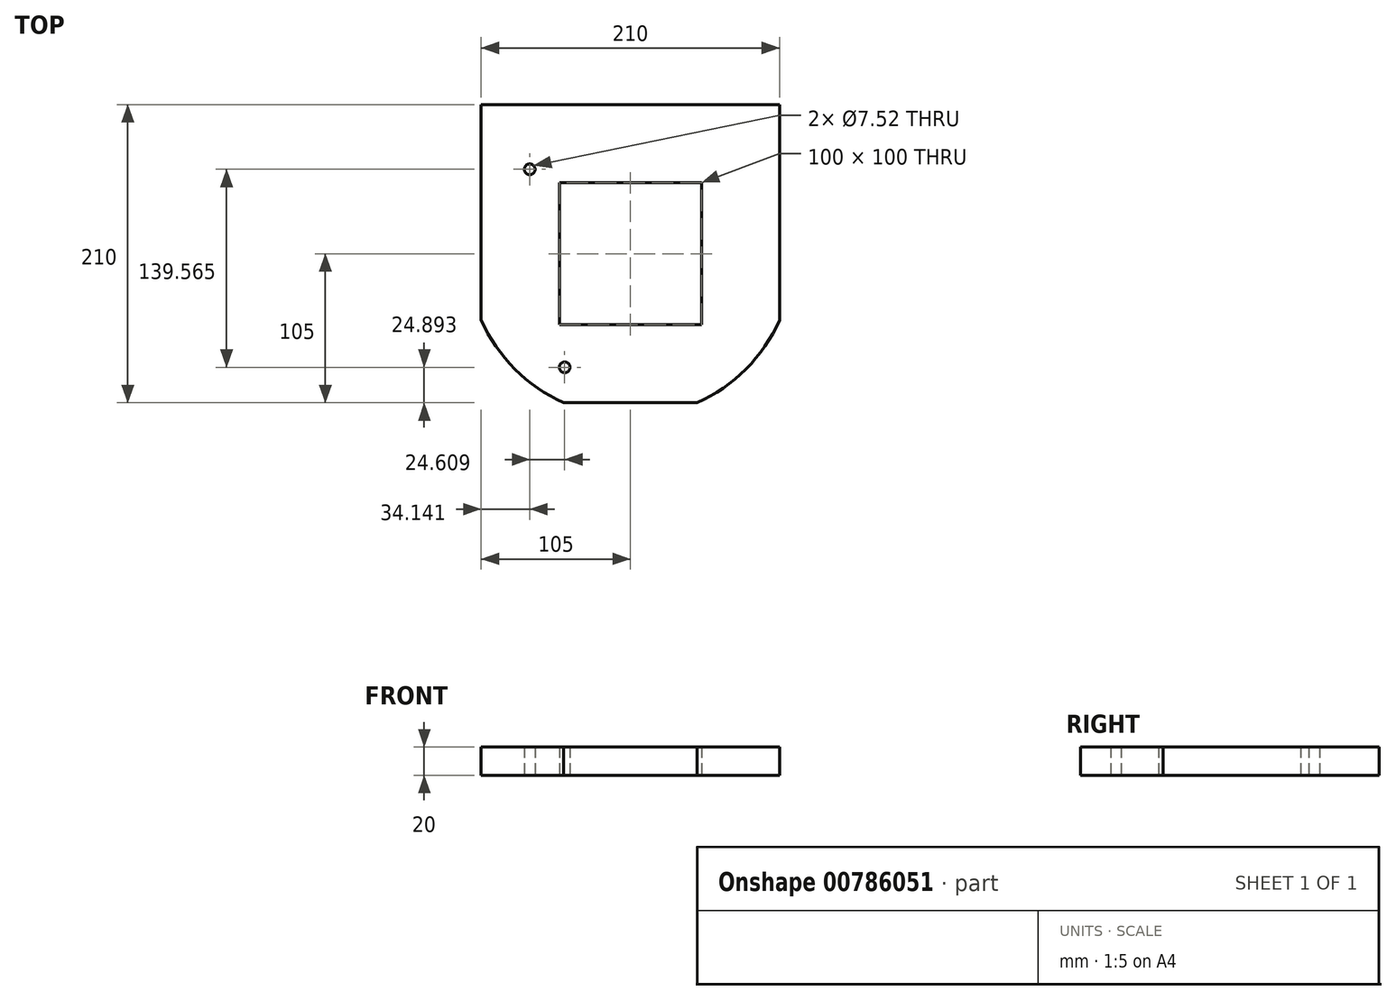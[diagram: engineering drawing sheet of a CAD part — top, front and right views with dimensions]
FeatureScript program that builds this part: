
annotation { "Feature Type Name" : "Feature", "Feature Type Description" : "" }
export const myFeature = defineFeature(function(context is Context, id is Id, definition is map)
    precondition{}
    {
        {
            var Q0;
            Q0=qCreatedBy(makeId("Top.planeOp"),FACE);
            var sketch = newSketch(context, id + "F0", { "sketchPlane" : qUnion([Q0])});
            skCircle(sketch, "E0", {"center": v(0, 0) * mm, "radius": 115 * mm});
            skCircle(sketch, "E1", {"center": v(0, 0) * mm, "radius": 15 * mm});
            skLineSegment(sketch, "E2.bottom", {"start": v(50, -50) * mm, "end": v(-50, -50) * mm});
            skLineSegment(sketch, "E2.top", {"start": v(50, 50) * mm, "end": v(-50, 50) * mm});
            skLineSegment(sketch, "E2.left", {"start": v(50, -50) * mm, "end": v(50, 50) * mm});
            skLineSegment(sketch, "E2.right", {"start": v(-50, -50) * mm, "end": v(-50, 50) * mm});
            skLineSegment(sketch, "E3.bottom", {"start": v(105, -105) * mm, "end": v(-105, -105) * mm});
            skLineSegment(sketch, "E3.top", {"start": v(105, 105) * mm, "end": v(-105, 105) * mm});
            skLineSegment(sketch, "E3.left", {"start": v(105, -105) * mm, "end": v(105, 105) * mm});
            skLineSegment(sketch, "E3.right", {"start": v(-105, -105) * mm, "end": v(-105, 105) * mm});
            skSolve(sketch);
        }
        {
            var Q0;
            {var subQ0=sQuery(id+"F0.wireOp",EDGE,"E3.top");var subQ1=sQuery(id+"F0.wireOp",EDGE,"E0");var subQ2=makeQuery(id+"F0.imprint","INTERSECT",VERTEX,{"disambiguationData":[OD(0.0)],"derivedFrom":[subQ1,subQ0]});Q0=makeQuery(id+"F0.imprint","IMPRINT",FACE,{"disambiguationData":[TD([[makeQuery(id+"F0.imprint","IMPRINT",EDGE,{"disambiguationData":[TD([[subQ2,1.0]])],"derivedFrom":subQ1}),-1.0]])]});}
            var Q1;
            {var subQ0=sQuery(id+"F0.wireOp",EDGE,"E3.top");var subQ1=sQuery(id+"F0.wireOp",EDGE,"E0");var subQ2=makeQuery(id+"F0.imprint","INTERSECT",VERTEX,{"disambiguationData":[OD(1.0)],"derivedFrom":[subQ1,subQ0]});Q1=makeQuery(id+"F0.imprint","IMPRINT",FACE,{"disambiguationData":[TD([[makeQuery(id+"F0.imprint","IMPRINT",EDGE,{"disambiguationData":[TD([[subQ2,-1.0]])],"derivedFrom":subQ1}),-1.0]])]});}
            var Q2;
            {var subQ0=sQuery(id+"F0.wireOp",EDGE,"E3.right");var subQ1=sQuery(id+"F0.wireOp",EDGE,"E0");var subQ2=makeQuery(id+"F0.imprint","INTERSECT",VERTEX,{"disambiguationData":[OD(1.0)],"derivedFrom":[subQ1,subQ0]});Q2=makeQuery(id+"F0.imprint","IMPRINT",FACE,{"disambiguationData":[TD([[makeQuery(id+"F0.imprint","IMPRINT",EDGE,{"disambiguationData":[TD([[subQ2,-1.0]])],"derivedFrom":subQ1}),-1.0]])]});}
            var Q3;
            {var subQ0=sQuery(id+"F0.wireOp",EDGE,"E3.bottom");var subQ1=sQuery(id+"F0.wireOp",EDGE,"E0");var subQ2=makeQuery(id+"F0.imprint","INTERSECT",VERTEX,{"disambiguationData":[OD(1.0)],"derivedFrom":[subQ1,subQ0]});Q3=makeQuery(id+"F0.imprint","IMPRINT",FACE,{"disambiguationData":[TD([[makeQuery(id+"F0.imprint","IMPRINT",EDGE,{"disambiguationData":[TD([[subQ2,-1.0]])],"derivedFrom":subQ1}),-1.0]])]});}
            var Q4;
            Q4=makeQuery(id+"F0.imprint","IMPRINT",FACE,{"disambiguationData":[TD([[makeQuery(id+"F0.imprint","IMPRINT",EDGE,{"derivedFrom":sQuery(id+"F0.wireOp",EDGE,"E2.bottom")}),1.0]])]});
            extrude(context, id + "F1", {"entities" : qUnion([Q0, Q1, Q2, Q3, Q4]), "depth" : 20 * mm, "offsetDistance" : 25 * mm});
        }
        {
            var Q0;
            Q0=qCreatedBy(makeId("Top.planeOp"),FACE);
            var sketch = newSketch(context, id + "F2", { "sketchPlane" : qUnion([Q0])});
            skCircle(sketch, "E4", {"center": v(0, 0) * mm, "radius": 92.5 * mm, "construction": true});
            skCircle(sketch, "E5", {"center": v(-70.86, 59.46) * mm, "radius": 3.76 * mm});
            skCircle(sketch, "E6", {"center": v(-46.25, -80.1) * mm, "radius": 3.76 * mm});
            skLineSegment(sketch, "E7", {"start": v(-70.86, 59.46) * mm, "end": v(0, 0) * mm, "construction": true});
            skLineSegment(sketch, "E8", {"start": v(0, 0) * mm, "end": v(-46.25, -80.1) * mm, "construction": true});
            skLineSegment(sketch, "E9", {"start": v(0, 0) * mm, "end": v(-92.5, 0) * mm, "construction": true});
            skLineSegment(sketch, "E10", {"start": v(0, 92.5) * mm, "end": v(0, -92.5) * mm, "construction": true});
            skCircle(sketch, "E11", {"center": v(92.5, 0) * mm, "radius": 3.76 * mm, "construction": true});
            skSolve(sketch);
        }
        {
            var Q0;
            Q0=qSketchRegion(id+"F2",true);
            extrude(context, id + "F3", {"entities" : qUnion([Q0]), "operationType" : NewBodyOperationType.REMOVE, "depth" : 25 * mm, "offsetDistance" : 25 * mm});
        }
    });
